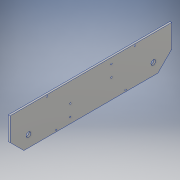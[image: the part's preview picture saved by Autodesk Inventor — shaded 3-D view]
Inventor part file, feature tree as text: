
AUTODESK INVENTOR PART (.ipt)
format: ipt  version: 2019 (Build 230136000, 136)  size: 151,552 bytes
history: native  units: in
note: dims shown in document units (in); Inventor stores cm internally (conversion verified against a paired STEP export)
features: chamfer x2, hole x2, sketch x2, projected_geometry x2, extrude x1
ambient origin geometry x8: Origin, YZ Plane, XZ Plane, XY Plane, X Axis, Y Axis, Z Axis, Center Point
bodies: Solid1 (feature_tree)
feature tree (9):
  extrude  "Extrusion1"  Depth=17.5in
  chamfer  "Chamfer1"  Distance=1.25in
  chamfer  "Chamfer2"  Distance=2.0in
  hole  "Hole1"  [1 undecoded]
  hole  "Hole2"  [1 undecoded]
  sketch  "Sketch1"  dims[d0=4.0in d1=17.5in]
  projected_geometry  "Projected Loop5"
  sketch  "Sketch7"  dims[d2=0.501in d3=1.25in d4=2.0in d5=2.0in d6=0.1875in d7=0.0in d8=1.5in d9=0.125in d10=45.0deg d11=1.5in d12=0.125in d13=45.0deg d22=6.517in d23=0.125in d24=0.603in d25=0.125in d26=0.63in d27=6.517in d28=0.125in d29=0.603in d30=6.517in d31=0.125in d32=0.63in d33=6.517in d80=1.26in d83=0.63in d86=1.26in d87=0.63in d88=0.15in d89=0.75in d90=0.375in d91=0.25in d92=0.5635in d93=1.0in d94=0.8108in d95=0.175in d96=0.175in d97=0.175in d98=0.175in d99=4.0in d100=4.0in d101=5.0in d102=5.0in d103=0.15in d104=0.75in d105=0.375in d106=0.25in d107=0.5635in d108=1.0in d109=0.8108in]
  projected_geometry  "Projected Loop6"
note: 2 required parameter values undecoded (feature->parameter linkage not recoverable at this tier; creation-order binding heuristic only, values carry confidence <= 0.55)
